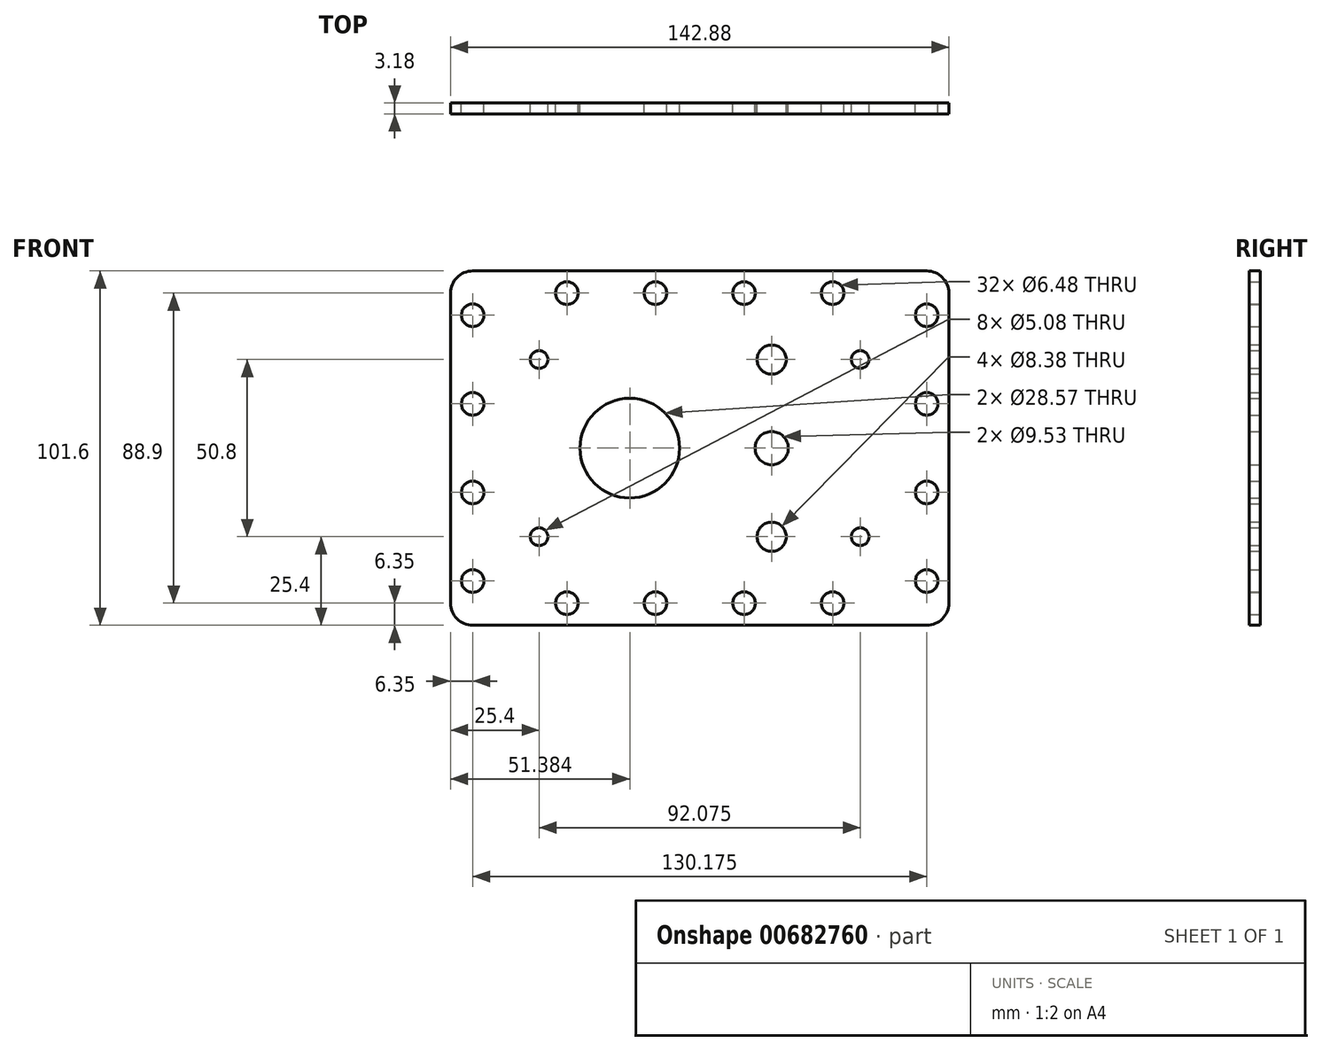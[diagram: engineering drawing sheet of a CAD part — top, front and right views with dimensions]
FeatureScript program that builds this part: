
annotation { "Feature Type Name" : "Feature", "Feature Type Description" : "" }
export const myFeature = defineFeature(function(context is Context, id is Id, definition is map)
    precondition{}
    {
        {
            var Q0;
            Q0=qCreatedBy(makeId("Front.planeOp"),FACE);
            var sketch = newSketch(context, id + "F0", { "sketchPlane" : qUnion([Q0])});
            skLineSegment(sketch, "E0.bottom", {"start": v(6.35, 0) * mm, "end": v(136.53, 0) * mm});
            skLineSegment(sketch, "E0.top", {"start": v(6.35, 101.6) * mm, "end": v(136.53, 101.6) * mm});
            skLineSegment(sketch, "E0.left", {"start": v(0, 6.35) * mm, "end": v(0, 95.25) * mm});
            skLineSegment(sketch, "E0.right", {"start": v(142.88, 6.35) * mm, "end": v(142.88, 95.25) * mm});
            skCircle(sketch, "E1", {"center": v(6.35, 88.9) * mm, "radius": 3.24 * mm});
            skCircle(sketch, "E2.0.1.0", {"center": v(6.35, 63.5) * mm, "radius": 3.24 * mm});
            skCircle(sketch, "E2.0.2.0", {"center": v(6.35, 38.1) * mm, "radius": 3.24 * mm});
            skCircle(sketch, "E2.0.3.0", {"center": v(6.35, 12.7) * mm, "radius": 3.24 * mm});
            skCircle(sketch, "E2.1.0.0", {"center": v(136.53, 88.9) * mm, "radius": 3.24 * mm});
            skCircle(sketch, "E2.1.1.0", {"center": v(136.53, 63.5) * mm, "radius": 3.24 * mm});
            skCircle(sketch, "E2.1.2.0", {"center": v(136.53, 38.1) * mm, "radius": 3.24 * mm});
            skCircle(sketch, "E2.1.3.0", {"center": v(136.53, 12.7) * mm, "radius": 3.24 * mm});
            skLineSegment(sketch, "E2.direction1", {"start": v(6.35, 88.9) * mm, "end": v(136.53, 88.9) * mm, "construction": true});
            skLineSegment(sketch, "E2.direction2", {"start": v(6.35, 88.9) * mm, "end": v(6.35, 63.5) * mm, "construction": true});
            skCircle(sketch, "E3", {"center": v(33.35, 95.25) * mm, "radius": 3.24 * mm});
            skCircle(sketch, "E4.0.1.0", {"center": v(33.35, 6.35) * mm, "radius": 3.24 * mm});
            skCircle(sketch, "E4.1.0.0", {"center": v(58.75, 95.25) * mm, "radius": 3.24 * mm});
            skCircle(sketch, "E4.1.1.0", {"center": v(58.75, 6.35) * mm, "radius": 3.24 * mm});
            skCircle(sketch, "E4.2.0.0", {"center": v(84.15, 95.25) * mm, "radius": 3.24 * mm});
            skCircle(sketch, "E4.2.1.0", {"center": v(84.15, 6.35) * mm, "radius": 3.24 * mm});
            skCircle(sketch, "E4.3.0.0", {"center": v(109.55, 95.25) * mm, "radius": 3.24 * mm});
            skCircle(sketch, "E4.3.1.0", {"center": v(109.55, 6.35) * mm, "radius": 3.24 * mm});
            skLineSegment(sketch, "E4.direction1", {"start": v(33.35, 95.25) * mm, "end": v(58.75, 95.25) * mm, "construction": true});
            skLineSegment(sketch, "E4.direction2", {"start": v(33.35, 95.25) * mm, "end": v(33.35, 6.35) * mm, "construction": true});
            skPoint(sketch, "E5.visualSharp", {"position": v(0, 101.6) * mm});
            skArc(sketch, "E5.filletArc", {"start": v(6.35, 101.6) * mm, "mid": v(1.86, 99.74) * mm, "end": v(0, 95.25) * mm});
            skPoint(sketch, "E6.visualSharp", {"position": v(0, 0) * mm});
            skArc(sketch, "E6.filletArc", {"start": v(0, 6.35) * mm, "mid": v(1.86, 1.86) * mm, "end": v(6.35, 0) * mm});
            skPoint(sketch, "E7.visualSharp", {"position": v(142.88, 0) * mm});
            skArc(sketch, "E7.filletArc", {"start": v(136.53, 0) * mm, "mid": v(141.02, 1.86) * mm, "end": v(142.88, 6.35) * mm});
            skPoint(sketch, "E8.visualSharp", {"position": v(142.88, 101.6) * mm});
            skArc(sketch, "E8.filletArc", {"start": v(142.88, 95.25) * mm, "mid": v(141.02, 99.74) * mm, "end": v(136.53, 101.6) * mm});
            skCircle(sketch, "E9", {"center": v(51.38, 50.8) * mm, "radius": 14.29 * mm});
            skCircle(sketch, "E10", {"center": v(92.08, 76.2) * mm, "radius": 4.2 * mm});
            skCircle(sketch, "E11", {"center": v(92.08, 50.8) * mm, "radius": 4.76 * mm});
            skCircle(sketch, "E12", {"center": v(92.08, 25.4) * mm, "radius": 4.2 * mm});
            skCircle(sketch, "E13", {"center": v(25.4, 76.2) * mm, "radius": 2.54 * mm});
            skCircle(sketch, "E14.0.1.0", {"center": v(25.4, 25.4) * mm, "radius": 2.54 * mm});
            skCircle(sketch, "E14.1.0.0", {"center": v(117.48, 76.2) * mm, "radius": 2.54 * mm});
            skCircle(sketch, "E14.1.1.0", {"center": v(117.48, 25.4) * mm, "radius": 2.54 * mm});
            skLineSegment(sketch, "E14.direction1", {"start": v(25.4, 76.2) * mm, "end": v(117.48, 76.2) * mm, "construction": true});
            skLineSegment(sketch, "E14.direction2", {"start": v(25.4, 76.2) * mm, "end": v(25.4, 25.4) * mm, "construction": true});
            skSolve(sketch);
        }
        {
            var Q0;
            Q0=makeQuery(id+"F0.imprint","IMPRINT",FACE,{"disambiguationData":[TD([[makeQuery(id+"F0.imprint","IMPRINT",EDGE,{"derivedFrom":sQuery(id+"F0.wireOp",EDGE,"E0.bottom")}),1.0]])]});
            extrude(context, id + "F1", {"entities" : qUnion([Q0]), "depth" : 3.17 * mm, "offsetDistance" : 25.4 * mm});
        }
    });
